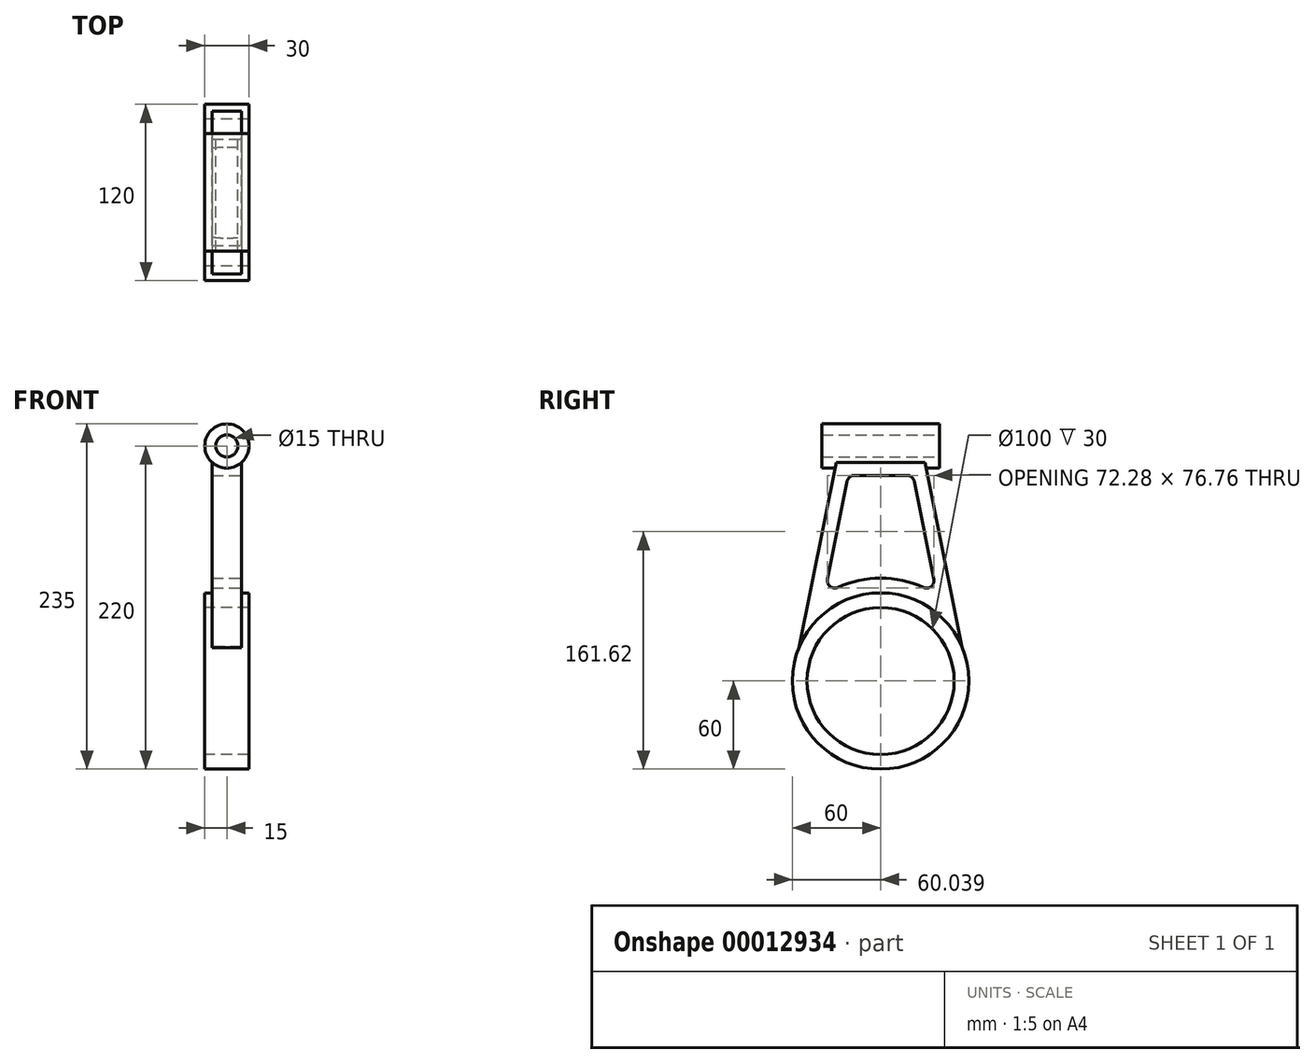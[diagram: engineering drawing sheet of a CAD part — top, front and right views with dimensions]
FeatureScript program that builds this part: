
annotation { "Feature Type Name" : "Feature", "Feature Type Description" : "" }
export const myFeature = defineFeature(function(context is Context, id is Id, definition is map)
    precondition{}
    {
        {
            var Q0;
            Q0=qCreatedBy(makeId("Right.planeOp"),FACE);
            var sketch = newSketch(context, id + "F0", { "sketchPlane" : qUnion([Q0])});
            skCircle(sketch, "E0", {"center": v(0, 0) * mm, "radius": 50 * mm});
            skCircle(sketch, "E1", {"center": v(0, 0) * mm, "radius": 60 * mm});
            skSolve(sketch);
        }
        {
            var Q0;
            Q0 = qSketchRegion(id + "F0", true);
            extrude(context, id + "F6", {"entities" : qUnion([Q0]), "endBound" : BoundingType.SYMMETRIC, "depth" : 30 * mm});
        }
        {
            var Q0;
            Q0=qCreatedBy(makeId("Right.planeOp"),FACE);
            cPlane(context, id + "F1", {"entities" : qUnion([Q0]), "cplaneType" : CPlaneType.OFFSET, "offset" : 10 * mm, "width" : 150 * mm, "height" : 150 * mm});
        }
        {
            var Q0;
            Q0=qCreatedBy(id+"F1.planeOp",FACE);
            var sketch = newSketch(context, id + "F2", { "sketchPlane" : qUnion([Q0])});
            skCircle(sketch, "E2", {"center": v(0, 0) * mm, "radius": 59.95 * mm});
            skLineSegment(sketch, "E3.0", {"start": v(30, 150) * mm, "end": v(55.4, 22.92) * mm});
            skLineSegment(sketch, "E4.0", {"start": v(-30, 150) * mm, "end": v(-55.57, 22.48) * mm});
            skLineSegment(sketch, "E5", {"start": v(30, 150) * mm, "end": v(-30, 150) * mm});
            skArc(sketch, "E6", {"start": v(29.11, 63.66) * mm, "mid": v(0.04, 70) * mm, "end": v(-29.04, 63.7) * mm});
            skLineSegment(sketch, "E7", {"start": v(36.1, 69.19) * mm, "end": v(22.75, 135.98) * mm});
            skLineSegment(sketch, "E8", {"start": v(17.85, 140) * mm, "end": v(-17.85, 140) * mm});
            skLineSegment(sketch, "E9", {"start": v(-22.75, 135.97) * mm, "end": v(-36.02, 69.22) * mm});
            skPoint(sketch, "E10.visualSharp", {"position": v(38.2, 58.66) * mm});
            skArc(sketch, "E10.filletArc", {"start": v(29.11, 63.66) * mm, "mid": v(34.3, 64.28) * mm, "end": v(36.1, 69.19) * mm});
            skPoint(sketch, "E11.visualSharp", {"position": v(-38.1, 58.72) * mm});
            skArc(sketch, "E11.filletArc", {"start": v(-36.02, 69.22) * mm, "mid": v(-34.22, 64.32) * mm, "end": v(-29.04, 63.7) * mm});
            skPoint(sketch, "E12.visualSharp", {"position": v(-21.95, 140) * mm});
            skArc(sketch, "E12.filletArc", {"start": v(-17.85, 140) * mm, "mid": v(-21.02, 138.86) * mm, "end": v(-22.75, 135.97) * mm});
            skPoint(sketch, "E13.visualSharp", {"position": v(21.95, 140) * mm});
            skArc(sketch, "E13.filletArc", {"start": v(22.75, 135.98) * mm, "mid": v(21.02, 138.87) * mm, "end": v(17.85, 140) * mm});
            skSolve(sketch);
        }
        {
            var Q0;
            {var subQ1=sQuery(id+"F2.wireOp",EDGE,"E3.0");Q0=makeQuery(id+"F2.imprint","IMPRINT",FACE,{"disambiguationData":[TD([[makeQuery(id+"F2.imprint","IMPRINT",EDGE,{"derivedFrom":subQ1}),-1.0]])]});}
            extrude(context, id + "F3", {"entities" : qUnion([Q0]), "operationType" : NewBodyOperationType.ADD, "oppositeDirection" : true, "depth" : 20 * mm});
        }
        {
            var Q0;
            Q0=qCreatedBy(makeId("Front.planeOp"),FACE);
            var sketch = newSketch(context, id + "F4", { "sketchPlane" : qUnion([Q0])});
            skLineSegment(sketch, "E14", {"start": v(0, 0) * mm, "end": v(0, 224.25) * mm, "construction": true});
            skCircle(sketch, "E15", {"center": v(0, 160) * mm, "radius": 15 * mm});
            skCircle(sketch, "E16", {"center": v(0, 160) * mm, "radius": 7.5 * mm});
            skSolve(sketch);
        }
        {
            var Q0;
            Q0=makeQuery(id+"F4.imprint","IMPRINT",FACE,{"disambiguationData":[TD([[makeQuery(id+"F4.imprint","IMPRINT",EDGE,{"derivedFrom":sQuery(id+"F4.wireOp",EDGE,"E15")}),1.0]])]});
            extrude(context, id + "F5", {"entities" : qUnion([Q0]), "operationType" : NewBodyOperationType.ADD, "endBound" : BoundingType.SYMMETRIC, "depth" : 80 * mm});
        }
    });
